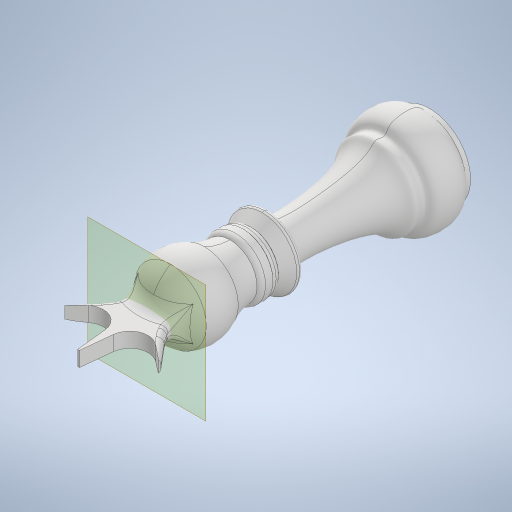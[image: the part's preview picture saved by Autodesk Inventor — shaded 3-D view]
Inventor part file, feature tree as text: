
AUTODESK INVENTOR PART (.ipt)
format: ipt  version: 2024.1 (Build 281209000, 209)  size: 782,336 bytes
history: native  units: mm
features: fillet x9, sketch x6, extrude x5, projected_geometry x4, chamfer x3, other x1, revolve x1, plane x1
ambient origin geometry x8: Origin, YZ Plane, XZ Plane, XY Plane, X Axis, Y Axis, Z Axis, Center Point
bodies: Solid1 (feature_tree)
feature tree (30):
  extrude  "Extrusion1"  Depth=10.0mm TaperAngle=0.0deg
  other  "Work Axis1"
  extrude  "Extrusion2"  Depth=14.3mm
  revolve  "Revolution1"  [1 undecoded]
  fillet  "Fillet2"  Radius=9.4mm
  chamfer  "Chamfer3"  Distance=10.36mm
  chamfer  "Chamfer4"  Distance=5.18mm
  fillet  "Fillet3"  Radius=12.3mm
  fillet  "Fillet4"  Radius=6.15mm
  fillet  "Fillet5"  Radius=2.2mm
  fillet  "Fillet9"  Radius=1.5mm
  plane  "Work Plane9"
  extrude  "Extrusion11"  Depth=1.0mm
  extrude  "Extrusion12"  Depth=1.0mm
  extrude  "Extrusion13"  Depth=1.0mm
  fillet  "Fillet10"  Radius=1.45mm
  chamfer  "Chamfer7"  Distance=1.0mm
  fillet  "Fillet11"  Radius=1.0mm
  fillet  "Fillet12"  Radius=0.6mm
  fillet  "Fillet13"  Radius=42.6mm
  sketch  "Sketch1"  dims[d0=10.0mm d1=3.0mm d2=0.0mm]
  sketch  "Sketch2"  dims[d5=360.0deg d6=14.3mm]
  sketch  "Sketch3"  dims[d7=3.0mm d8=0.0mm d74=13.55mm d81=9.4mm]
  projected_geometry  "Projected Loop1"
  sketch  "Sketch16"  dims[d82=4.7mm]
  sketch  "Sketch17"  dims[d84=10.56mm]
  sketch  "Sketch18"  dims[d85=5.28mm d87=10.36mm d88=5.18mm d89=12.3mm d90=6.15mm d91=2.2mm d92=1.5mm d93=2.03mm d98=1.0mm d99=0.1mm d100=3.17mm d101=6.108652mm d102=1.45mm d103=2.0mm d104=6.108652mm d105=1.0mm d106=1.0mm d107=0.6mm d127=42.6mm d128=10.0mm d129=1.3mm d130=1.3mm d133=2.0mm d134=0.0mm d135=2.0mm d136=0.0mm d137=10.0mm d138=1.5mm d139=2.0mm d140=45.0deg d141=6.4mm d142=2.133333mm d143=2.133333mm d144=2.133333mm d145=3.2mm d146=3.2mm d147=0.2mm d148=0.0mm d149=8.726646mm d150=3.2mm d151=0.3mm d152=2.0mm d153=0.0mm d154=3.0mm d155=1.0mm d156=2.0mm]
  projected_geometry  "Projected Loop3"
  projected_geometry  "Projected Loop4"
  projected_geometry  "Projected Loop5"
note: 1 required parameter value undecoded (feature->parameter linkage not recoverable at this tier; creation-order binding heuristic only, values carry confidence <= 0.55)
